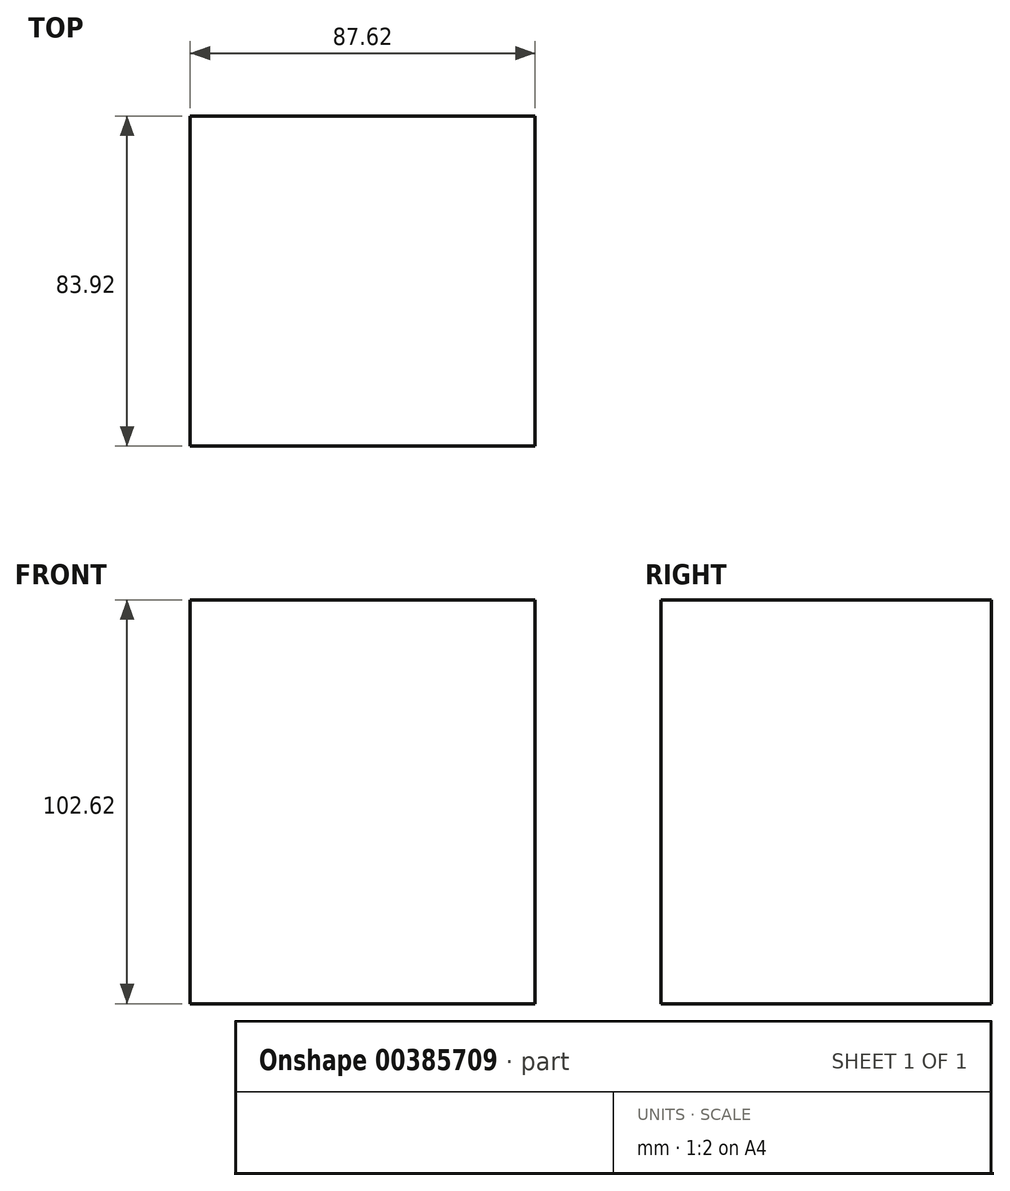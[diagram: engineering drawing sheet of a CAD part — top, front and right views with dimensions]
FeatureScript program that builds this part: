
annotation { "Feature Type Name" : "Feature", "Feature Type Description" : "" }
export const myFeature = defineFeature(function(context is Context, id is Id, definition is map)
    precondition{}
    {
        {
            var Q0;
            Q0=qCreatedBy(makeId("Top.planeOp"),FACE);
            var sketch = newSketch(context, id + "F0", { "sketchPlane" : qUnion([Q0])});
            skLineSegment(sketch, "E0.bottom", {"start": v(43.8, 41.96) * mm, "end": v(-43.8, 41.96) * mm});
            skLineSegment(sketch, "E0.top", {"start": v(43.8, -41.96) * mm, "end": v(-43.8, -41.96) * mm});
            skLineSegment(sketch, "E0.left", {"start": v(43.8, 41.96) * mm, "end": v(43.8, -41.96) * mm});
            skLineSegment(sketch, "E0.right", {"start": v(-43.8, 41.96) * mm, "end": v(-43.8, -41.96) * mm});
            skPoint(sketch, "E0.middle", {"position": v(0, 0) * mm});
            skSolve(sketch);
        }
        {
            var Q0;
            Q0=makeQuery(id+"F0.imprint","IMPRINT",FACE,{"disambiguationData":[TD([[makeQuery(id+"F0.imprint","IMPRINT",EDGE,{"derivedFrom":sQuery(id+"F0.wireOp",EDGE,"E0.bottom")}),1.0]])]});
            extrude(context, id + "F1", {"entities" : qUnion([Q0]), "depth" : 102.62 * mm});
        }
        {
            var Q0;
            Q0=makeQuery(id+"F1.opExtrude","SWEPT_FACE",FACE,{"disambiguationData":[OSD([sQuery(id+"F0.wireOp",EDGE,"E0.left")])]});
            var sketch = newSketch(context, id + "F2", { "sketchPlane" : qUnion([Q0])});
            skCircle(sketch, "E1", {"center": v(22.59, 83.72) * mm, "radius": 7.6 * mm});
            skSolve(sketch);
        }
        {
            var Q0;
            Q0=makeQuery(id+"F2.imprint","IMPRINT",FACE,{"disambiguationData":[TD([[makeQuery(id+"F2.imprint","IMPRINT",EDGE,{"derivedFrom":sQuery(id+"F2.wireOp",EDGE,"E1")}),1.0]])]});
            var Q1;
            Q1=sQuery(id+"F2.wireOp",EDGE,"E1");
            var Q2;
            Q2=makeQuery(id+"F1.opExtrude","CAP_EDGE",EDGE,{"disambiguationData":[OSD([sQuery(id+"F0.wireOp",EDGE,"E0.right")])],"isStart":false});
            var Q3;
            Q3=makeQuery(id+"F1.opExtrude","CAP_EDGE",EDGE,{"disambiguationData":[OSD([sQuery(id+"F0.wireOp",EDGE,"E0.top")])],"isStart":false});
            var Q4;
            Q4=makeQuery(id+"F1.opExtrude","CAP_EDGE",EDGE,{"disambiguationData":[OSD([sQuery(id+"F0.wireOp",EDGE,"E0.bottom")])],"isStart":false});
            sweep(context, id + "F3", {"bodyType" : ToolBodyType.SURFACE, "profiles" : qUnion([Q0]), "surfaceProfiles" : qUnion([Q1]), "path" : qUnion([Q2, Q3, Q4])});
        }
    });
